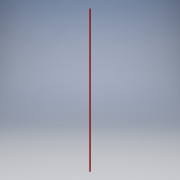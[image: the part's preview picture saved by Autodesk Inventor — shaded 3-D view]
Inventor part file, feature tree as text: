
AUTODESK INVENTOR PART (.ipt)
format: ipt  version: 2016 (Build 200138000, 138)  size: 100,352 bytes
history: native  units: in
note: dims shown in document units (in); Inventor stores cm internally (conversion verified against a paired STEP export)
features: extrude x1, sketch x1
ambient origin geometry x8: Origin, YZ Plane, XZ Plane, XY Plane, X Axis, Y Axis, Z Axis, Center Point
bodies: Solid1 (feature_tree)
feature tree (2):
  extrude  "Extrusion1"  Depth=70.8661in TaperAngle=0.0deg
  sketch  "Sketch1"  dims[d0=0.3937in d1=70.8661in d2=0.0in]
